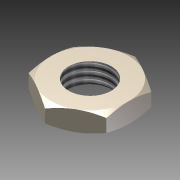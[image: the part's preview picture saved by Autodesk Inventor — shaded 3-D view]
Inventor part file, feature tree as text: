
AUTODESK INVENTOR PART (.ipt)
format: ipt  version: 2012 (Build 160160000, 160)  size: 260,096 bytes
history: native  units: in
note: dims shown in document units (in); Inventor stores cm internally (conversion verified against a paired STEP export)
features: plane x2, split x2, other x1, hole x1, thread x1, imported_body x1, sketch x1
ambient origin geometry x8: Origin, YZ Plane, XZ Plane, XY Plane, X Axis, Y Axis, Z Axis, Center Point
bodies: Solid1 (feature_tree)
feature tree (9):
  other  "KQ2LU04-M6.SAT1"
  plane  "Work Plane1"
  plane  "Work Plane2"
  split  "Split1"
  split  "Split2"
  hole  "Hole1"  [1 undecoded]
  thread  "Thread1"  [1 undecoded]
  imported_body  "Base1"
  sketch  "Sketch1"  dims[d0=0.0in d1=0.0in d2=0.2362in d3=0.2362in d4=0.2362in d5=0.1575in d6=0.0787in d7=90.0deg d8=0.315in d9=0.8108in d10=0.3937in d11=0.0in]
note: 2 required parameter values undecoded (feature->parameter linkage not recoverable at this tier; creation-order binding heuristic only, values carry confidence <= 0.55)
